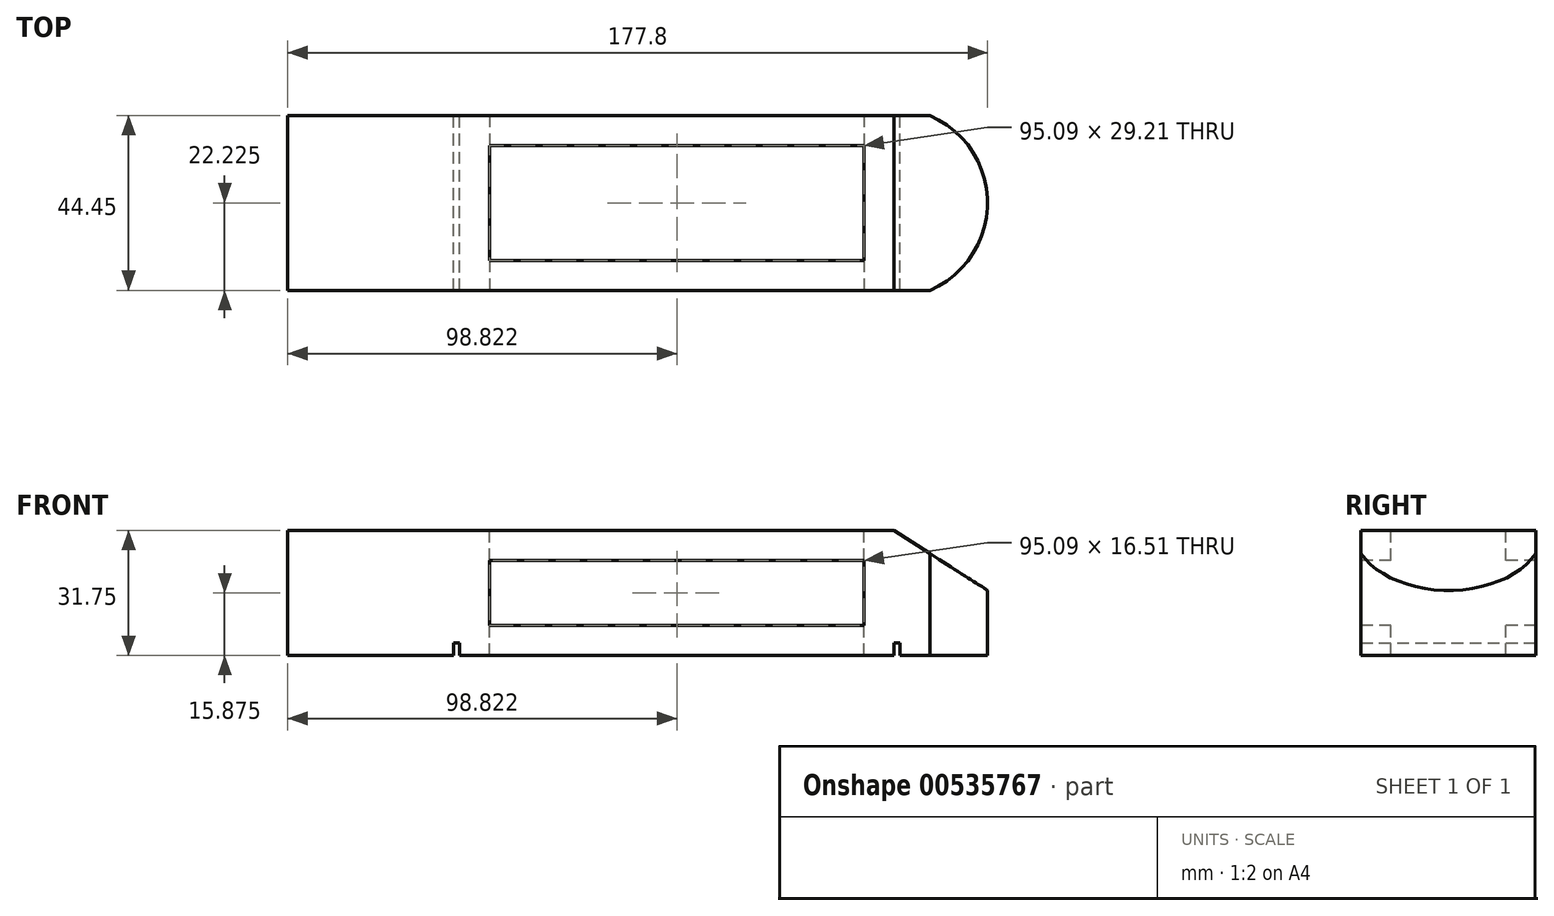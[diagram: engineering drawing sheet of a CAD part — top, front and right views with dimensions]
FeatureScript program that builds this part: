
annotation { "Feature Type Name" : "Feature", "Feature Type Description" : "" }
export const myFeature = defineFeature(function(context is Context, id is Id, definition is map)
    precondition{}
    {
        {
            var Q0;
            Q0=qCreatedBy(makeId("Top.planeOp"),FACE);
            var sketch = newSketch(context, id + "F0", { "sketchPlane" : qUnion([Q0])});
            skLineSegment(sketch, "E0.bottom", {"start": v(0, 0) * mm, "end": v(-177.8, 0) * mm});
            skLineSegment(sketch, "E0.top", {"start": v(0, -44.45) * mm, "end": v(-177.8, -44.45) * mm});
            skLineSegment(sketch, "E0.left", {"start": v(0, 0) * mm, "end": v(0, -44.45) * mm});
            skLineSegment(sketch, "E0.right", {"start": v(-177.8, 0) * mm, "end": v(-177.8, -44.45) * mm});
            skSolve(sketch);
        }
        {
            var Q0;
            Q0=makeQuery(id+"F0.imprint","IMPRINT",FACE,{"disambiguationData":[TD([[makeQuery(id+"F0.imprint","IMPRINT",EDGE,{"derivedFrom":sQuery(id+"F0.wireOp",EDGE,"E0.bottom")}),1.0]])]});
            extrude(context, id + "F1", {"entities" : qUnion([Q0]), "depth" : 31.75 * mm});
        }
        {
            var Q0;
            Q0=makeQuery(id+"F1.opExtrude","CAP_FACE",FACE,{"disambiguationData":[OSD([sQuery(id+"F0.wireOp",EDGE,"E0.bottom"),sQuery(id+"F0.wireOp",EDGE,"E0.top"),sQuery(id+"F0.wireOp",EDGE,"E0.left"),sQuery(id+"F0.wireOp",EDGE,"E0.right")])],"isStart":true});
            var sketch = newSketch(context, id + "F2", { "sketchPlane" : qUnion([Q0])});
            skLineSegment(sketch, "E1.bottom", {"start": v(-135.73, 44.45) * mm, "end": v(-134.14, 44.45) * mm});
            skLineSegment(sketch, "E1.top", {"start": v(-135.73, 0) * mm, "end": v(-134.14, 0) * mm});
            skLineSegment(sketch, "E1.left", {"start": v(-135.73, 44.45) * mm, "end": v(-135.73, 0) * mm});
            skLineSegment(sketch, "E1.right", {"start": v(-134.14, 44.45) * mm, "end": v(-134.14, 0) * mm});
            skLineSegment(sketch, "E2.bottom", {"start": v(-23.81, 44.45) * mm, "end": v(-22.23, 44.45) * mm});
            skLineSegment(sketch, "E2.top", {"start": v(-23.81, 0) * mm, "end": v(-22.23, 0) * mm});
            skLineSegment(sketch, "E2.left", {"start": v(-23.81, 44.45) * mm, "end": v(-23.81, 0) * mm});
            skLineSegment(sketch, "E2.right", {"start": v(-22.23, 44.45) * mm, "end": v(-22.23, 0) * mm});
            skSolve(sketch);
        }
        {
            var Q0;
            Q0=makeQuery(id+"F2.imprint","IMPRINT",FACE,{"disambiguationData":[TD([[makeQuery(id+"F2.imprint","IMPRINT",EDGE,{"derivedFrom":sQuery(id+"F2.wireOp",EDGE,"E2.bottom")}),1.0]])]});
            var Q1;
            Q1=makeQuery(id+"F2.imprint","IMPRINT",FACE,{"disambiguationData":[TD([[makeQuery(id+"F2.imprint","IMPRINT",EDGE,{"derivedFrom":sQuery(id+"F2.wireOp",EDGE,"E1.bottom")}),1.0]])]});
            extrude(context, id + "F3", {"entities" : qUnion([Q0, Q1]), "operationType" : NewBodyOperationType.REMOVE, "oppositeDirection" : true, "depth" : 3.17 * mm});
        }
        {
            var Q0;
            Q0=makeQuery(id+"F1.opExtrude","CAP_FACE",FACE,{"disambiguationData":[OSD([sQuery(id+"F0.wireOp",EDGE,"E0.bottom"),sQuery(id+"F0.wireOp",EDGE,"E0.top"),sQuery(id+"F0.wireOp",EDGE,"E0.left"),sQuery(id+"F0.wireOp",EDGE,"E0.right")])],"isStart":false});
            var sketch = newSketch(context, id + "F4", { "sketchPlane" : qUnion([Q0])});
            skLineSegment(sketch, "E3.bottom", {"start": v(-31.43, -7.62) * mm, "end": v(-126.52, -7.62) * mm});
            skLineSegment(sketch, "E3.top", {"start": v(-31.43, -36.83) * mm, "end": v(-126.52, -36.83) * mm});
            skLineSegment(sketch, "E3.left", {"start": v(-31.43, -7.62) * mm, "end": v(-31.43, -36.83) * mm});
            skLineSegment(sketch, "E3.right", {"start": v(-126.52, -7.62) * mm, "end": v(-126.52, -36.83) * mm});
            skSolve(sketch);
        }
        {
            var Q0;
            Q0=makeQuery(id+"F4.imprint","IMPRINT",FACE,{"disambiguationData":[TD([[makeQuery(id+"F4.imprint","IMPRINT",EDGE,{"derivedFrom":sQuery(id+"F4.wireOp",EDGE,"E3.bottom")}),1.0]])]});
            extrude(context, id + "F5", {"entities" : qUnion([Q0]), "operationType" : NewBodyOperationType.REMOVE, "endBound" : BoundingType.THROUGH_ALL, "oppositeDirection" : true, "depth" : 25.4 * mm, "offsetDistance" : 25.4 * mm});
        }
        {
            var Q0;
            Q0=makeQuery(id+"F1.opExtrude","SWEPT_FACE",FACE,{"disambiguationData":[OSD([sQuery(id+"F0.wireOp",EDGE,"E0.top")])]});
            var sketch = newSketch(context, id + "F6", { "sketchPlane" : qUnion([Q0])});
            skLineSegment(sketch, "E4.bottom", {"start": v(-126.52, 24.13) * mm, "end": v(-31.43, 24.13) * mm});
            skLineSegment(sketch, "E4.top", {"start": v(-126.52, 7.62) * mm, "end": v(-31.43, 7.62) * mm});
            skLineSegment(sketch, "E4.left", {"start": v(-126.52, 24.13) * mm, "end": v(-126.52, 7.62) * mm});
            skLineSegment(sketch, "E4.right", {"start": v(-31.43, 24.13) * mm, "end": v(-31.43, 7.62) * mm});
            skSolve(sketch);
        }
        {
            var Q0;
            Q0 = qSketchRegion(id + "F6", true);
            extrude(context, id + "F7", {"entities" : qUnion([Q0]), "operationType" : NewBodyOperationType.REMOVE, "endBound" : BoundingType.THROUGH_ALL, "oppositeDirection" : true, "depth" : 25.4 * mm, "offsetDistance" : 25.4 * mm});
        }
        {
            var Q0;
            Q0=makeQuery(id+"F1.opExtrude","CAP_FACE",FACE,{"disambiguationData":[OSD([sQuery(id+"F0.wireOp",EDGE,"E0.bottom"),sQuery(id+"F0.wireOp",EDGE,"E0.top"),sQuery(id+"F0.wireOp",EDGE,"E0.left"),sQuery(id+"F0.wireOp",EDGE,"E0.right")])],"isStart":false});
            var sketch = newSketch(context, id + "F8", { "sketchPlane" : qUnion([Q0])});
            skArc(sketch, "E5", {"start": v(-14.6, -44.45) * mm, "mid": v(0, -22.23) * mm, "end": v(-14.6, 0) * mm});
            skLineSegment(sketch, "E6", {"start": v(-14.6, -44.45) * mm, "end": v(0, -44.45) * mm});
            skLineSegment(sketch, "E7", {"start": v(0, -44.45) * mm, "end": v(0, 0) * mm});
            skLineSegment(sketch, "E8", {"start": v(0, 0) * mm, "end": v(-14.6, 0) * mm});
            skSolve(sketch);
        }
        {
            var Q0;
            Q0 = qSketchRegion(id + "F8", true);
            extrude(context, id + "F9", {"entities" : qUnion([Q0]), "operationType" : NewBodyOperationType.REMOVE, "endBound" : BoundingType.THROUGH_ALL, "oppositeDirection" : true, "depth" : 25.4 * mm, "offsetDistance" : 25.4 * mm});
        }
        {
            var Q0;
            Q0=makeQuery(id+"F1.opExtrude","SWEPT_FACE",FACE,{"disambiguationData":[OSD([sQuery(id+"F0.wireOp",EDGE,"E0.bottom")])]});
            var sketch = newSketch(context, id + "F10", { "sketchPlane" : qUnion([Q0])});
            skLineSegment(sketch, "E9", {"start": v(23.81, 31.75) * mm, "end": v(0, 16.5) * mm});
            skLineSegment(sketch, "E10", {"start": v(0, 16.51) * mm, "end": v(0, 31.75) * mm});
            skLineSegment(sketch, "E11", {"start": v(0, 31.75) * mm, "end": v(23.81, 31.75) * mm});
            skSolve(sketch);
        }
        {
            var Q0;
            Q0 = qSketchRegion(id + "F10", true);
            extrude(context, id + "F11", {"entities" : qUnion([Q0]), "operationType" : NewBodyOperationType.REMOVE, "endBound" : BoundingType.THROUGH_ALL, "oppositeDirection" : true, "depth" : 25.4 * mm, "offsetDistance" : 25.4 * mm});
        }
    });
